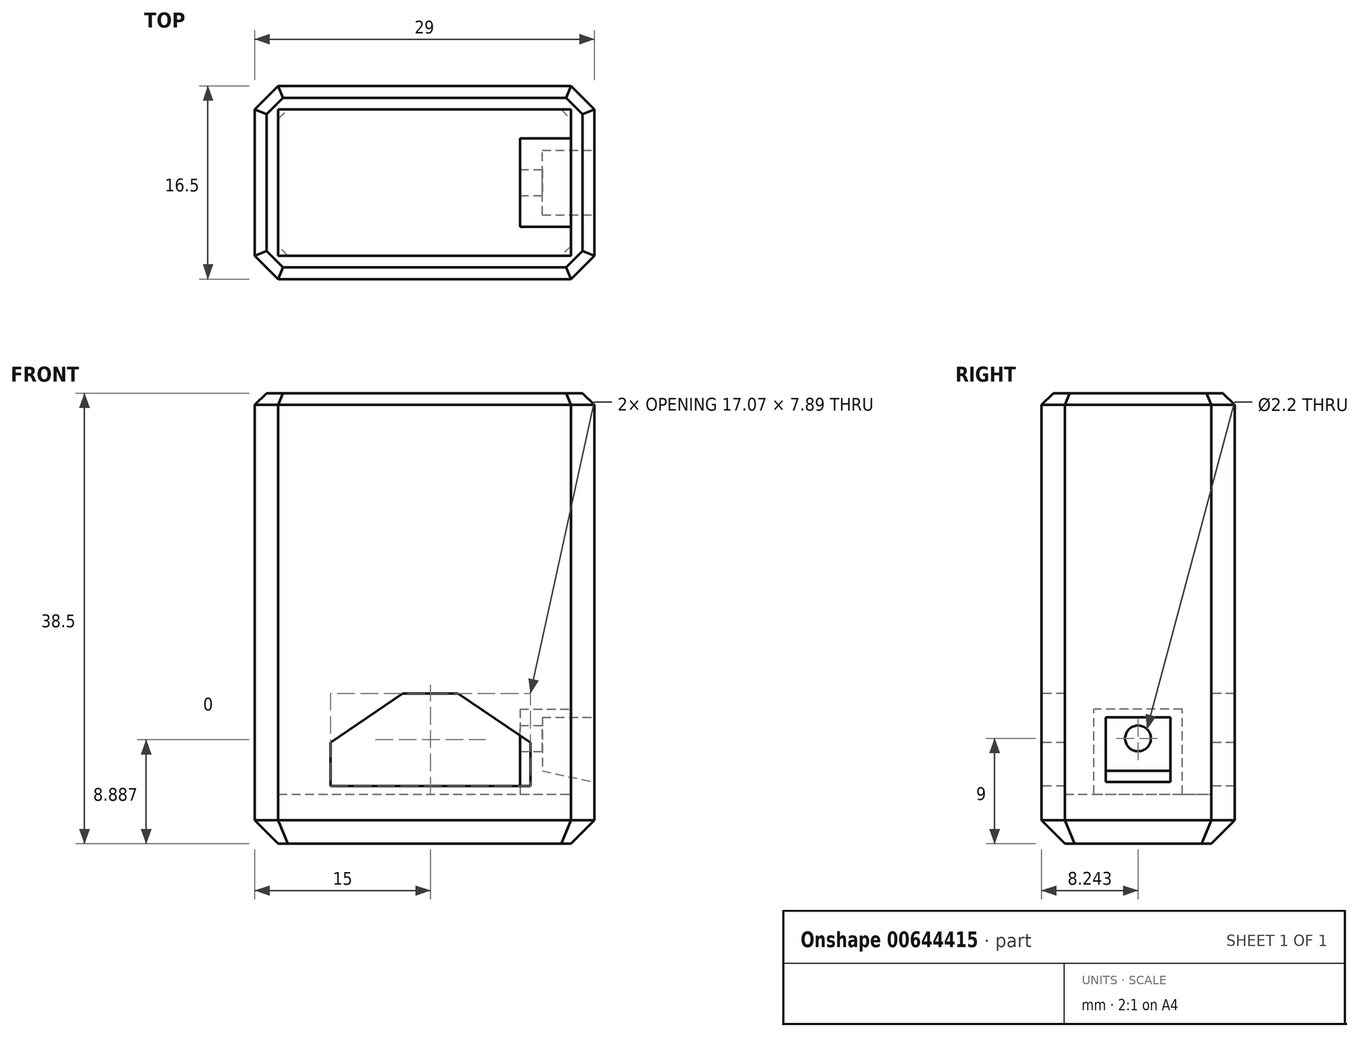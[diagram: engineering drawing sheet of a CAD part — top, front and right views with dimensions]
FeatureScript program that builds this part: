
annotation { "Feature Type Name" : "Feature", "Feature Type Description" : "" }
export const myFeature = defineFeature(function(context is Context, id is Id, definition is map)
    precondition{}
    {
        {
            var Q0;
            Q0=qCreatedBy(makeId("Top.planeOp"),FACE);
            var sketch = newSketch(context, id + "F0", { "sketchPlane" : qUnion([Q0])});
            skLineSegment(sketch, "E0.bottom", {"start": v(0, 0) * mm, "end": v(29, 0) * mm});
            skLineSegment(sketch, "E0.top", {"start": v(0, 16.5) * mm, "end": v(29, 16.5) * mm});
            skLineSegment(sketch, "E0.left", {"start": v(0, 0) * mm, "end": v(0, 16.5) * mm});
            skLineSegment(sketch, "E0.right", {"start": v(29, 0) * mm, "end": v(29, 16.5) * mm});
            skSolve(sketch);
        }
        {
            var Q0;
            Q0=makeQuery(id+"F0.imprint","IMPRINT",FACE,{"disambiguationData":[TD([[makeQuery(id+"F0.imprint","IMPRINT",EDGE,{"derivedFrom":sQuery(id+"F0.wireOp",EDGE,"E0.bottom")}),1.0]])]});
            extrude(context, id + "F1", {"entities" : qUnion([Q0]), "depth" : 38.5 * mm, "offsetDistance" : 25 * mm});
        }
        {
            var Q0;
            Q0=makeQuery(id+"F1.opExtrude","CAP_FACE",FACE,{"disambiguationData":[OSD([sQuery(id+"F0.wireOp",EDGE,"E0.bottom"),sQuery(id+"F0.wireOp",EDGE,"E0.top"),sQuery(id+"F0.wireOp",EDGE,"E0.left"),sQuery(id+"F0.wireOp",EDGE,"E0.right")])],"isStart":false});
            shell(context, id + "F2", {"entities" : qUnion([Q0]), "thickness" : 2 * mm});
        }
        {
            var Q0;
            Q0=makeQuery(id+"F2.opShell","OFFSET_FACE",FACE,{"disambiguationData":[OSD([sQuery(id+"F0.wireOp",EDGE,"E0.bottom"),sQuery(id+"F0.wireOp",EDGE,"E0.top"),sQuery(id+"F0.wireOp",EDGE,"E0.left"),sQuery(id+"F0.wireOp",EDGE,"E0.right")])]});
            extrude(context, id + "F3", {"entities" : qUnion([Q0]), "operationType" : NewBodyOperationType.ADD, "depth" : 2.25 * mm, "offsetDistance" : 25 * mm});
        }
        {
            var Q0;
            Q0=makeQuery(id+"F1.opExtrude","SWEPT_EDGE",EDGE,{"disambiguationData":[OSD([sQuery(id+"F0.wireOp",EDGE,"E0.bottom"),sQuery(id+"F0.wireOp",EDGE,"E0.right")])]});
            var Q1;
            Q1=makeQuery(id+"F1.opExtrude","SWEPT_EDGE",EDGE,{"disambiguationData":[OSD([sQuery(id+"F0.wireOp",EDGE,"E0.top"),sQuery(id+"F0.wireOp",EDGE,"E0.right")])]});
            var Q2;
            Q2=makeQuery(id+"F1.opExtrude","SWEPT_EDGE",EDGE,{"disambiguationData":[OSD([sQuery(id+"F0.wireOp",EDGE,"E0.top"),sQuery(id+"F0.wireOp",EDGE,"E0.left")])]});
            var Q3;
            Q3=makeQuery(id+"F1.opExtrude","SWEPT_EDGE",EDGE,{"disambiguationData":[OSD([sQuery(id+"F0.wireOp",EDGE,"E0.bottom"),sQuery(id+"F0.wireOp",EDGE,"E0.left")])]});
            chamfer(context, id + "F4", {"entities" : qUnion([Q0, Q1, Q2, Q3]), "width" : 2 * mm, "tangentPropagation" : true});
        }
        {
            var Q0;
            Q0=makeQuery(id+"F1.opExtrude","CAP_FACE",FACE,{"disambiguationData":[OSD([sQuery(id+"F0.wireOp",EDGE,"E0.bottom"),sQuery(id+"F0.wireOp",EDGE,"E0.top"),sQuery(id+"F0.wireOp",EDGE,"E0.left"),sQuery(id+"F0.wireOp",EDGE,"E0.right")])],"isStart":true});
            chamfer(context, id + "F5", {"entities" : qUnion([Q0]), "width" : 2 * mm, "tangentPropagation" : true});
        }
        {
            var Q0;
            Q0=makeQuery(id+"F1.opExtrude","CAP_EDGE",EDGE,{"disambiguationData":[OSD([sQuery(id+"F0.wireOp",EDGE,"E0.bottom")])],"isStart":false});
            var Q1;
            {var subQ0=sQuery(id+"F0.wireOp",EDGE,"E0.right");var subQ1=sQuery(id+"F0.wireOp",EDGE,"E0.bottom");Q1=makeQuery(id+"F4.opChamfer","BLEND_EDGE",EDGE,{"blendedFrom":[makeQuery(id+"F1.opExtrude","SWEPT_EDGE",EDGE,{"disambiguationData":[OSD([subQ1,subQ0])]}),makeQuery(id+"F1.opExtrude","CAP_FACE",FACE,{"disambiguationData":[OSD([subQ1,sQuery(id+"F0.wireOp",EDGE,"E0.top"),sQuery(id+"F0.wireOp",EDGE,"E0.left"),subQ0])],"isStart":false})],"blendedInto":[makeQuery(id+"F1.opExtrude","CAP_FACE",FACE,{"disambiguationData":[OSD([subQ1,sQuery(id+"F0.wireOp",EDGE,"E0.top"),sQuery(id+"F0.wireOp",EDGE,"E0.left"),subQ0])],"isStart":false})]});}
            var Q2;
            Q2=makeQuery(id+"F1.opExtrude","CAP_EDGE",EDGE,{"disambiguationData":[OSD([sQuery(id+"F0.wireOp",EDGE,"E0.right")])],"isStart":false});
            var Q3;
            {var subQ0=sQuery(id+"F0.wireOp",EDGE,"E0.right");var subQ1=sQuery(id+"F0.wireOp",EDGE,"E0.top");Q3=makeQuery(id+"F4.opChamfer","BLEND_EDGE",EDGE,{"blendedFrom":[makeQuery(id+"F1.opExtrude","SWEPT_EDGE",EDGE,{"disambiguationData":[OSD([subQ1,subQ0])]}),makeQuery(id+"F1.opExtrude","CAP_FACE",FACE,{"disambiguationData":[OSD([sQuery(id+"F0.wireOp",EDGE,"E0.bottom"),subQ1,sQuery(id+"F0.wireOp",EDGE,"E0.left"),subQ0])],"isStart":false})],"blendedInto":[makeQuery(id+"F1.opExtrude","CAP_FACE",FACE,{"disambiguationData":[OSD([sQuery(id+"F0.wireOp",EDGE,"E0.bottom"),subQ1,sQuery(id+"F0.wireOp",EDGE,"E0.left"),subQ0])],"isStart":false})]});}
            var Q4;
            Q4=makeQuery(id+"F1.opExtrude","CAP_EDGE",EDGE,{"disambiguationData":[OSD([sQuery(id+"F0.wireOp",EDGE,"E0.top")])],"isStart":false});
            var Q5;
            {var subQ0=sQuery(id+"F0.wireOp",EDGE,"E0.left");var subQ1=sQuery(id+"F0.wireOp",EDGE,"E0.top");Q5=makeQuery(id+"F4.opChamfer","BLEND_EDGE",EDGE,{"blendedFrom":[makeQuery(id+"F1.opExtrude","SWEPT_EDGE",EDGE,{"disambiguationData":[OSD([subQ1,subQ0])]}),makeQuery(id+"F1.opExtrude","CAP_FACE",FACE,{"disambiguationData":[OSD([sQuery(id+"F0.wireOp",EDGE,"E0.bottom"),subQ1,subQ0,sQuery(id+"F0.wireOp",EDGE,"E0.right")])],"isStart":false})],"blendedInto":[makeQuery(id+"F1.opExtrude","CAP_FACE",FACE,{"disambiguationData":[OSD([sQuery(id+"F0.wireOp",EDGE,"E0.bottom"),subQ1,subQ0,sQuery(id+"F0.wireOp",EDGE,"E0.right")])],"isStart":false})]});}
            var Q6;
            Q6=makeQuery(id+"F1.opExtrude","CAP_EDGE",EDGE,{"disambiguationData":[OSD([sQuery(id+"F0.wireOp",EDGE,"E0.left")])],"isStart":false});
            var Q7;
            {var subQ0=sQuery(id+"F0.wireOp",EDGE,"E0.left");var subQ1=sQuery(id+"F0.wireOp",EDGE,"E0.bottom");Q7=makeQuery(id+"F4.opChamfer","BLEND_EDGE",EDGE,{"blendedFrom":[makeQuery(id+"F1.opExtrude","SWEPT_EDGE",EDGE,{"disambiguationData":[OSD([subQ1,subQ0])]}),makeQuery(id+"F1.opExtrude","CAP_FACE",FACE,{"disambiguationData":[OSD([subQ1,sQuery(id+"F0.wireOp",EDGE,"E0.top"),subQ0,sQuery(id+"F0.wireOp",EDGE,"E0.right")])],"isStart":false})],"blendedInto":[makeQuery(id+"F1.opExtrude","CAP_FACE",FACE,{"disambiguationData":[OSD([subQ1,sQuery(id+"F0.wireOp",EDGE,"E0.top"),subQ0,sQuery(id+"F0.wireOp",EDGE,"E0.right")])],"isStart":false})]});}
            chamfer(context, id + "F6", {"entities" : qUnion([Q0, Q1, Q2, Q3, Q4, Q5, Q6, Q7]), "width" : 1 * mm, "tangentPropagation" : true});
        }
        {
            var Q0;
            Q0=makeQuery(id+"F1.opExtrude","SWEPT_FACE",FACE,{"disambiguationData":[OSD([sQuery(id+"F0.wireOp",EDGE,"E0.bottom")])]});
            var sketch = newSketch(context, id + "F7", { "sketchPlane" : qUnion([Q0])});
            skLineSegment(sketch, "E1", {"start": v(6.46, 4.94) * mm, "end": v(23.54, 4.94) * mm});
            skLineSegment(sketch, "E2", {"start": v(23.54, 4.94) * mm, "end": v(23.54, 8.66) * mm});
            skLineSegment(sketch, "E3", {"start": v(23.54, 8.66) * mm, "end": v(17.36, 12.83) * mm});
            skLineSegment(sketch, "E4", {"start": v(17.36, 12.83) * mm, "end": v(12.64, 12.83) * mm});
            skLineSegment(sketch, "E5", {"start": v(12.64, 12.83) * mm, "end": v(6.46, 8.66) * mm});
            skLineSegment(sketch, "E6", {"start": v(6.46, 8.66) * mm, "end": v(6.46, 4.94) * mm});
            skSolve(sketch);
        }
        {
            var Q0;
            Q0 = qSketchRegion(id + "F7", true);
            extrude(context, id + "F8", {"entities" : qUnion([Q0]), "operationType" : NewBodyOperationType.REMOVE, "endBound" : BoundingType.THROUGH_ALL, "oppositeDirection" : true, "depth" : 25 * mm, "offsetDistance" : 25 * mm});
        }
        {
            var Q0;
            Q0=makeQuery(id+"F1.opExtrude","SWEPT_FACE",FACE,{"disambiguationData":[OSD([sQuery(id+"F0.wireOp",EDGE,"E0.right")])]});
            var sketch = newSketch(context, id + "F9", { "sketchPlane" : qUnion([Q0])});
            skLineSegment(sketch, "E7.bottom", {"start": v(4.48, 11.5) * mm, "end": v(12.02, 11.5) * mm});
            skLineSegment(sketch, "E7.top", {"start": v(4.48, 4.25) * mm, "end": v(12.02, 4.25) * mm});
            skLineSegment(sketch, "E7.left", {"start": v(4.48, 11.5) * mm, "end": v(4.48, 4.25) * mm});
            skLineSegment(sketch, "E7.right", {"start": v(12.02, 11.5) * mm, "end": v(12.02, 4.25) * mm});
            skCircle(sketch, "E8", {"center": v(8.24, 9) * mm, "radius": 1.1 * mm});
            skSolve(sketch);
        }
        {
            var Q0;
            Q0=makeQuery(id+"F9.imprint","IMPRINT",FACE,{"disambiguationData":[TD([[makeQuery(id+"F9.imprint","IMPRINT",EDGE,{"derivedFrom":sQuery(id+"F9.wireOp",EDGE,"E7.bottom")}),-1.0]])]});
            extrude(context, id + "F10", {"entities" : qUnion([Q0]), "operationType" : NewBodyOperationType.ADD, "oppositeDirection" : true, "depth" : 6.35 * mm, "offsetDistance" : 25 * mm});
        }
        {
            var Q0;
            Q0=makeQuery(id+"F1.opExtrude","SWEPT_FACE",FACE,{"disambiguationData":[OSD([sQuery(id+"F0.wireOp",EDGE,"E0.right")])]});
            var sketch = newSketch(context, id + "F11", { "sketchPlane" : qUnion([Q0])});
            skLineSegment(sketch, "E9.bottom", {"start": v(5.48, 10.8) * mm, "end": v(11.02, 10.8) * mm});
            skLineSegment(sketch, "E9.top", {"start": v(5.48, 5.27) * mm, "end": v(11.02, 5.27) * mm});
            skLineSegment(sketch, "E9.left", {"start": v(5.48, 10.8) * mm, "end": v(5.48, 5.27) * mm});
            skLineSegment(sketch, "E9.right", {"start": v(11.02, 10.8) * mm, "end": v(11.02, 5.27) * mm});
            skSolve(sketch);
        }
        {
            var Q0;
            Q0=makeQuery(id+"F11.imprint","IMPRINT",FACE,{"disambiguationData":[TD([[makeQuery(id+"F11.imprint","IMPRINT",EDGE,{"derivedFrom":sQuery(id+"F11.wireOp",EDGE,"E9.bottom")}),1.0]])]});
            cPlane(context, id + "F12", {"entities" : qUnion([Q0]), "cplaneType" : CPlaneType.OFFSET, "offset" : 4.45 * mm, "oppositeDirection" : true, "width" : 150 * mm, "height" : 150 * mm});
        }
        {
            var Q0;
            Q0=qCreatedBy(id+"F12.planeOp",FACE);
            var sketch = newSketch(context, id + "F13", { "sketchPlane" : qUnion([Q0])});
            skLineSegment(sketch, "E10.bottom", {"start": v(5.48, 10.8) * mm, "end": v(11.02, 10.8) * mm});
            skLineSegment(sketch, "E10.top", {"start": v(5.48, 6.22) * mm, "end": v(11.02, 6.22) * mm});
            skLineSegment(sketch, "E10.left", {"start": v(5.48, 10.8) * mm, "end": v(5.48, 6.22) * mm});
            skLineSegment(sketch, "E10.right", {"start": v(11.02, 10.8) * mm, "end": v(11.02, 6.22) * mm});
            skSolve(sketch);
        }
        {
            var Q1;
            Q1 = qSketchRegion(id + "F13", true);
            var Q2;
            Q2 = qSketchRegion(id + "F11", true);
            loft(context, id + "F14", {"operationType" : NewBodyOperationType.REMOVE, "sheetProfilesArray" : [{ "sheetProfileEntities" : qUnion([Q1]) }, { "sheetProfileEntities" : qUnion([Q2]) }]});
        }
    });
